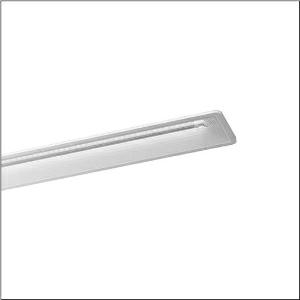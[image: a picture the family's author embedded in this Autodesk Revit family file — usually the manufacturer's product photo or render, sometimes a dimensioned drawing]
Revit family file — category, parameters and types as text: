
# Revit family: taris_r__21_5mt116d03wd_9457
name_source: partatom
category: Lighting Fixtures
units: mm (PartAtom-declared; Revit-internal decimal feet)

## family parameters
Cut with Voids When Loaded = No
Host = Face
Light Source = No
Part Type = Normal
Room Calculation Point = No
Round Connector Dimension = Use Diameter
Shared = No

## types (1)
- --- (1 x LED, 4560 lm, 28.9 W, 3000K)
    Apparent Load = 29 VA
    CIE Flux Codes = 73 96 99 100 100
    Color Rendering = 80
    Color Temperature = 3000K
    Default Elevation = 1800 mm
    Description = Taris® 21, office luminaire, primary anti-glare with micro louvre, primary optical cover: axial lens, of PMMA, structured, CAT 2 (L<= 1500cd/m²), light emission: direct distribution, primary light characteristic: symmetric, installation type: recessed, LED, rated luminous flux: 4.560lm, luminous efficacy: 158lm/W, light colour: 830, colour temperature: 3000K, control gear: ECG DALI, with terminal, 5-pole, mains connection: 230V, AC, 50Hz, rated input power: 29W, housing, luminaire housing, of plastic, traffic white (RAL 9016), module: M625, length: 1.250mm, width: 150mm, height: 76mm, recess depth: 106mm, protection rating (complete): IP20, insulation class (complete): insulation class I (protective earthing), certification: CE, ENEC, VDE, protection symbol: F, impact resistance: IK02, permissible operating ambient temperature: 0..+35°C, standard: EN 50419, packaging unit: 1 piece
    Height = 0 mm  [stored 0 ft]
    Lamp = 1 x LED
    Lamp Light Flux = 4560 lm
    Lamp Power = 28.9 W
    Lamp count = 1
    Length = 1243 mm
    Luminous efficacy = 158 lm/W
    Manufacturer = Siteco
    ModVariant = No
    Model = 5MT116D03WD
    Mounting Place = Ceiling
    Mounting Type = Recessed
    Number of Poles = 1
    OnlyDefault = Yes
    Power Factor = 1
    Product Name = Taris® 21
    Product group = office luminaire | ceiling recessed
    ProductGroupID = 401
    Protection Class = Protection class I
    Protection Degree = IP 20
    RLX_Detail_Level = 1
    RLX_Emergency_Light_Flux = 0 lm
    RLX_Emergency_Type = 0
    RLX_Emergency_Type_DB = No
    RlxData = <blob elided: 29989 chars, md5=a82577f1>
    Socket = socket
    Standby Power = 0 W
    System Light Flux = 4560 lm
    System Power = 29 W
    Type Comments = factory setting: luminous flux: 100 % | dim-lin: 254 | 200 mA
    Type Image = l_1004723.jpg
    URL = http://relux.com
    VarID = @adj_137019
    Voltage = 0 V
    Weight = 0.00 kg
    Width = 144 mm

note: [stored X ft] marks values corroborated as IEEE doubles in the binary element streams (Revit-internal decimal feet)

## geometry (parser evidence)
native form markers: Blend x4, Sweep x11
no freeform markers — native parametric forms only
